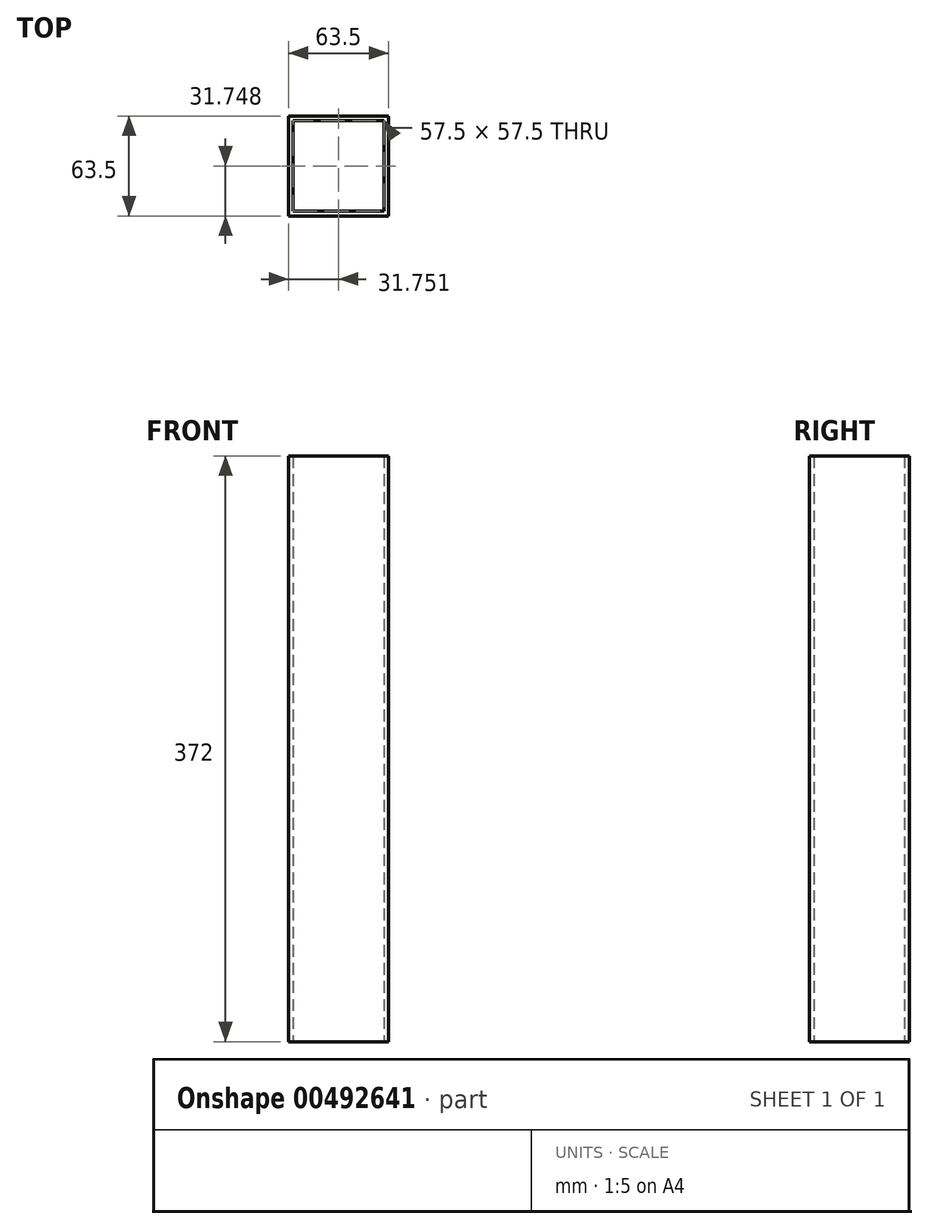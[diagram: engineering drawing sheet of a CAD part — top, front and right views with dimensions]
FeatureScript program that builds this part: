
annotation { "Feature Type Name" : "Feature", "Feature Type Description" : "" }
export const myFeature = defineFeature(function(context is Context, id is Id, definition is map)
    precondition{}
    {
        {
            var Q0;
            Q0=qCreatedBy(makeId("Top.planeOp"),FACE);
            var sketch = newSketch(context, id + "F0", { "sketchPlane" : qUnion([Q0])});
            skLineSegment(sketch, "E0.bottom", {"start": v(-27.08, 37.92) * mm, "end": v(36.42, 37.92) * mm});
            skLineSegment(sketch, "E0.top", {"start": v(-27.08, -25.58) * mm, "end": v(36.42, -25.58) * mm});
            skLineSegment(sketch, "E0.left", {"start": v(-27.08, 37.92) * mm, "end": v(-27.08, -25.58) * mm});
            skLineSegment(sketch, "E0.right", {"start": v(36.42, 37.92) * mm, "end": v(36.42, -25.58) * mm});
            skLineSegment(sketch, "E1.bottom", {"start": v(-24.08, 34.92) * mm, "end": v(33.42, 34.92) * mm});
            skLineSegment(sketch, "E1.top", {"start": v(-24.08, -22.58) * mm, "end": v(33.42, -22.58) * mm});
            skLineSegment(sketch, "E1.left", {"start": v(-24.08, 34.92) * mm, "end": v(-24.08, -22.58) * mm});
            skLineSegment(sketch, "E1.right", {"start": v(33.42, 34.92) * mm, "end": v(33.42, -22.58) * mm});
            skSolve(sketch);
        }
        {
            var Q0;
            Q0=qSketchRegion(id+"F0",true);
            extrude(context, id + "F1", {"entities" : qUnion([Q0]), "offsetDistance" : 25 * mm, "depth" : 372 * mm});
        }
    });
